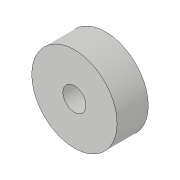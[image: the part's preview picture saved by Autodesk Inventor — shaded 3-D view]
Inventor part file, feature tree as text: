
AUTODESK INVENTOR PART (.ipt)
format: ipt  version: 2018.3 (Build 223284000, 284)  size: 81,408 bytes
history: native  units: in
note: dims shown in document units (in); Inventor stores cm internally (conversion verified against a paired STEP export)
features: extrude x1, sketch x1
ambient origin geometry x8: Origin, YZ Plane, XZ Plane, XY Plane, X Axis, Y Axis, Z Axis, Center Point
bodies: Solid1 (feature_tree)
feature tree (2):
  extrude  "Extrusion1"  Depth=0.251in
  sketch  "Sketch1"  dims[d0=0.186in d1=0.6875in d2=0.251in d3=0.0in]
